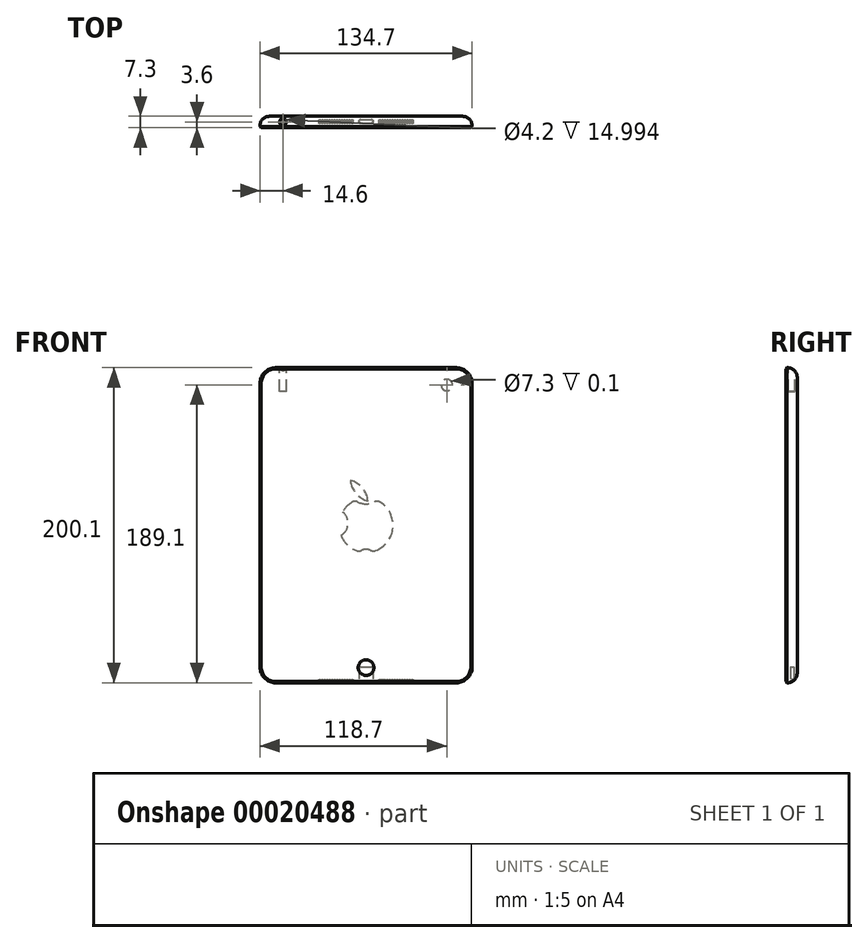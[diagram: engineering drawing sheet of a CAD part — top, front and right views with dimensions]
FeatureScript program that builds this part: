
annotation { "Feature Type Name" : "Feature", "Feature Type Description" : "" }
export const myFeature = defineFeature(function(context is Context, id is Id, definition is map)
    precondition{}
    {
        {
            var Q0;
            Q0=qCreatedBy(makeId("Front.planeOp"),FACE);
            var sketch = newSketch(context, id + "F0", { "sketchPlane" : qUnion([Q0])});
            skLineSegment(sketch, "E0.rect.bottom", {"start": v(-57.35, 100.05) * mm, "end": v(57.35, 100.05) * mm});
            skLineSegment(sketch, "E0.rect.top", {"start": v(-57.35, -100.05) * mm, "end": v(57.35, -100.05) * mm});
            skLineSegment(sketch, "E0.rect.left", {"start": v(-67.35, 90.05) * mm, "end": v(-67.35, -90.05) * mm});
            skLineSegment(sketch, "E0.rect.right", {"start": v(67.35, 90.05) * mm, "end": v(67.35, -90.05) * mm});
            skPoint(sketch, "E0.rect.middle", {"position": v(0, 0) * mm});
            skPoint(sketch, "E1.visualSharp", {"position": v(-67.35, 100.05) * mm});
            skArc(sketch, "E1.filletArc", {"start": v(-57.35, 100.05) * mm, "mid": v(-64.42, 97.12) * mm, "end": v(-67.35, 90.05) * mm});
            skPoint(sketch, "E2.visualSharp", {"position": v(67.35, 100.05) * mm});
            skArc(sketch, "E2.filletArc", {"start": v(67.35, 90.05) * mm, "mid": v(64.42, 97.12) * mm, "end": v(57.35, 100.05) * mm});
            skPoint(sketch, "E3.visualSharp", {"position": v(67.35, -100.05) * mm});
            skArc(sketch, "E3.filletArc", {"start": v(57.35, -100.05) * mm, "mid": v(64.42, -97.12) * mm, "end": v(67.35, -90.05) * mm});
            skPoint(sketch, "E4.visualSharp", {"position": v(-67.35, -100.05) * mm});
            skArc(sketch, "E4.filletArc", {"start": v(-67.35, -90.05) * mm, "mid": v(-64.42, -97.12) * mm, "end": v(-57.35, -100.05) * mm});
            skSolve(sketch);
        }
        {
            var Q0;
            Q0 = qSketchRegion(id + "F0", true);
            extrude(context, id + "F1", {"entities" : qUnion([Q0]), "endBound" : BoundingType.SYMMETRIC, "depth" : 7.2 * mm});
        }
        {
            var Q0;
            Q0=makeQuery(id+"F1.opExtrude","CAP_FACE",FACE,{"disambiguationData":[OSD([sQuery(id+"F0.wireOp",EDGE,"E0.rect.bottom"),sQuery(id+"F0.wireOp",EDGE,"E0.rect.top"),sQuery(id+"F0.wireOp",EDGE,"E0.rect.left"),sQuery(id+"F0.wireOp",EDGE,"E0.rect.right")])],"isStart":false});
            var sketch = newSketch(context, id + "F2", { "sketchPlane" : qUnion([Q0])});
            skLineSegment(sketch, "E5.rect.bottom", {"start": v(-60.65, 80.65) * mm, "end": v(60.65, 80.65) * mm});
            skLineSegment(sketch, "E5.rect.top", {"start": v(-60.65, -80.65) * mm, "end": v(60.65, -80.65) * mm});
            skLineSegment(sketch, "E5.rect.left", {"start": v(-60.65, 80.65) * mm, "end": v(-60.65, -80.65) * mm});
            skLineSegment(sketch, "E5.rect.right", {"start": v(60.65, 80.65) * mm, "end": v(60.65, -80.65) * mm});
            skPoint(sketch, "E5.rect.middle", {"position": v(0, 0) * mm});
            skCircle(sketch, "E6", {"center": v(0, 89.35) * mm, "radius": 1.2 * mm});
            skSolve(sketch);
        }
        {
            var Q0;
            Q0=makeQuery(id+"F2.imprint","IMPRINT",FACE,{"disambiguationData":[TD([[makeQuery(id+"F2.imprint","IMPRINT",EDGE,{"derivedFrom":sQuery(id+"F2.wireOp",EDGE,"E5.rect.bottom")}),-1.0]])]});
            var sketch = newSketch(context, id + "F3", { "sketchPlane" : qUnion([Q0])});
            skCircle(sketch, "E7", {"center": v(0, -90.45) * mm, "radius": 5 * mm});
            skSolve(sketch);
        }
        {
            var Q0;
            Q0=makeQuery(id+"F1.opExtrude","SWEPT_FACE",FACE,{"disambiguationData":[OSD([sQuery(id+"F0.wireOp",EDGE,"E0.rect.bottom")])]});
            var sketch = newSketch(context, id + "F4", { "sketchPlane" : qUnion([Q0])});
            skCircle(sketch, "E8", {"center": v(-52.75, 0) * mm, "radius": 2.1 * mm});
            skPoint(sketch, "E8.centerSnap0", {"position": v(57.35, 0) * mm});
            skSolve(sketch);
        }
        {
            var Q0;
            Q0=qCreatedBy(makeId("Top.planeOp"),FACE);
            cPlane(context, id + "F5", {"entities" : qUnion([Q0]), "cplaneType" : CPlaneType.OFFSET, "offset" : 90.45 * mm, "oppositeDirection" : true, "width" : 150 * mm, "height" : 150 * mm});
        }
        {
            var Q0;
            Q0=qCreatedBy(id+"F5.planeOp",FACE);
            var sketch = newSketch(context, id + "F6", { "sketchPlane" : qUnion([Q0])});
            skLineSegment(sketch, "E9.0", {"start": v(5, -3.6) * mm, "end": v(-5, -3.6) * mm});
            skArc(sketch, "E10", {"start": v(5, -3.6) * mm, "mid": v(2.51, -3.2) * mm, "end": v(0, -3.08) * mm});
            skLineSegment(sketch, "E11", {"start": v(0, -3.6) * mm, "end": v(0, -3.08) * mm});
            skLineSegment(sketch, "E12", {"start": v(0, -3.6) * mm, "end": v(5, -3.6) * mm});
            skSolve(sketch);
        }
        {
            var Q0;
            Q0=makeQuery(id+"F6.imprint","IMPRINT",FACE,{"disambiguationData":[TD([[makeQuery(id+"F6.imprint","IMPRINT",EDGE,{"derivedFrom":sQuery(id+"F6.wireOp",EDGE,"E10")}),1.0]])]});
            var Q1;
            Q1=sQuery(id+"F3.wireOp",EDGE,"E7");
            revolve(context, id + "F7", {"operationType" : NewBodyOperationType.REMOVE, "entities" : qUnion([Q0]), "axis" : qUnion([Q1]), "revolveType" : RevolveType.FULL, "oppositeDirection" : true});
        }
        {
            var Q0;
            Q0=makeQuery(id+"F1.opExtrude","CAP_FACE",FACE,{"disambiguationData":[OSD([sQuery(id+"F0.wireOp",EDGE,"E0.rect.bottom"),sQuery(id+"F0.wireOp",EDGE,"E0.rect.top"),sQuery(id+"F0.wireOp",EDGE,"E0.rect.left"),sQuery(id+"F0.wireOp",EDGE,"E0.rect.right"),sQuery(id+"F0.wireOp",EDGE,"E1.filletArc"),sQuery(id+"F0.wireOp",EDGE,"E2.filletArc"),sQuery(id+"F0.wireOp",EDGE,"E3.filletArc"),sQuery(id+"F0.wireOp",EDGE,"E4.filletArc")])],"isStart":true});
            var sketch = newSketch(context, id + "F8", { "sketchPlane" : qUnion([Q0])});
            skCircle(sketch, "E13", {"center": v(-51.35, 89.05) * mm, "radius": 3.65 * mm});
            skSolve(sketch);
        }
        {
            var Q0;
            Q0 = qSketchRegion(id + "F8", true);
            extrude(context, id + "F9", {"entities" : qUnion([Q0]), "operationType" : NewBodyOperationType.REMOVE, "oppositeDirection" : true, "depth" : 0.1 * mm});
        }
        {
            var Q0;
            Q0=makeQuery(id+"F1.opExtrude","CAP_EDGE",EDGE,{"disambiguationData":[OSD([sQuery(id+"F0.wireOp",EDGE,"E0.rect.left")])],"isStart":false});
            chamfer(context, id + "F10", {"entities" : qUnion([Q0]), "width" : 0.75 * mm, "tangentPropagation" : true});
        }
        {
            var Q0;
            Q0=makeQuery(id+"F1.opExtrude","CAP_EDGE",EDGE,{"disambiguationData":[OSD([sQuery(id+"F0.wireOp",EDGE,"E0.rect.bottom")])],"isStart":true});
            var Q1;
            Q1=makeQuery(id+"F1.opExtrude","CAP_EDGE",EDGE,{"disambiguationData":[OSD([sQuery(id+"F0.wireOp",EDGE,"E0.rect.left")])],"isStart":true});
            var Q2;
            Q2=makeQuery(id+"F1.opExtrude","CAP_EDGE",EDGE,{"disambiguationData":[OSD([sQuery(id+"F0.wireOp",EDGE,"E0.rect.right")])],"isStart":true});
            var Q3;
            Q3=makeQuery(id+"F1.opExtrude","CAP_EDGE",EDGE,{"disambiguationData":[OSD([sQuery(id+"F0.wireOp",EDGE,"E0.rect.top")])],"isStart":true});
            fillet(context, id + "F11", {"entities" : qUnion([Q0, Q1, Q2, Q3]), "radius" : 6 * mm, "tangentPropagation" : true, "allowEdgeOverflow" : false});
        }
        {
            var Q0;
            Q0=makeQuery(id+"F1.opExtrude","SWEPT_FACE",FACE,{"disambiguationData":[OSD([sQuery(id+"F0.wireOp",EDGE,"E0.rect.top")])]});
            var sketch = newSketch(context, id + "F12", { "sketchPlane" : qUnion([Q0])});
            skLineSegment(sketch, "E14.rect.bottom", {"start": v(-3.5, 0.85) * mm, "end": v(3.5, 0.85) * mm});
            skLineSegment(sketch, "E14.rect.top", {"start": v(-3.5, -1.45) * mm, "end": v(3.5, -1.45) * mm});
            skLineSegment(sketch, "E14.rect.left", {"start": v(-4.5, -0.15) * mm, "end": v(-4.5, -0.45) * mm});
            skLineSegment(sketch, "E14.rect.right", {"start": v(4.5, -0.15) * mm, "end": v(4.5, -0.45) * mm});
            skPoint(sketch, "E14.rect.middle", {"position": v(0, -0.3) * mm});
            skPoint(sketch, "E14.rect.middle.positionSnap0", {"position": v(0, 3.6) * mm});
            skPoint(sketch, "E14.rect.centerSnap0", {"position": v(0, 3.6) * mm});
            skPoint(sketch, "E15.visualSharp", {"position": v(-4.5, 0.85) * mm});
            skArc(sketch, "E15.filletArc", {"start": v(-3.5, 0.85) * mm, "mid": v(-4.2, 0.55) * mm, "end": v(-4.5, -0.15) * mm});
            skPoint(sketch, "E16.visualSharp", {"position": v(-4.5, -1.45) * mm});
            skArc(sketch, "E16.filletArc", {"start": v(-4.5, -0.45) * mm, "mid": v(-4.2, -1.16) * mm, "end": v(-3.5, -1.45) * mm});
            skPoint(sketch, "E17.visualSharp", {"position": v(4.5, 0.85) * mm});
            skArc(sketch, "E17.filletArc", {"start": v(4.5, -0.15) * mm, "mid": v(4.2, 0.55) * mm, "end": v(3.5, 0.85) * mm});
            skPoint(sketch, "E18.visualSharp", {"position": v(4.5, -1.45) * mm});
            skArc(sketch, "E18.filletArc", {"start": v(3.5, -1.45) * mm, "mid": v(4.2, -1.16) * mm, "end": v(4.5, -0.45) * mm});
            skSolve(sketch);
        }
        {
            var Q0;
            Q0=makeQuery(id+"F12.imprint","IMPRINT",FACE,{"disambiguationData":[TD([[makeQuery(id+"F12.imprint","IMPRINT",EDGE,{"derivedFrom":sQuery(id+"F12.wireOp",EDGE,"E14.rect.bottom")}),-1.0]])]});
            extrude(context, id + "F13", {"entities" : qUnion([Q0]), "operationType" : NewBodyOperationType.REMOVE, "oppositeDirection" : true, "depth" : 10 * mm});
        }
        {
            var Q0;
            Q0 = qSketchRegion(id + "F4", true);
            extrude(context, id + "F14", {"entities" : qUnion([Q0]), "operationType" : NewBodyOperationType.REMOVE, "oppositeDirection" : true, "depth" : 15 * mm});
        }
        {
            var Q0;
            {var subQ0=sQuery(id+"F0.wireOp",EDGE,"E0.rect.top");Q0=makeQuery(id+"F11.opFillet","BLEND_EDGE",EDGE,{"blendedFrom":[makeQuery(id+"F1.opExtrude","CAP_EDGE",EDGE,{"disambiguationData":[OSD([subQ0])],"isStart":true}),makeQuery(id+"F1.opExtrude","CAP_FACE",FACE,{"disambiguationData":[OSD([sQuery(id+"F0.wireOp",EDGE,"E0.rect.bottom"),subQ0,sQuery(id+"F0.wireOp",EDGE,"E0.rect.left"),sQuery(id+"F0.wireOp",EDGE,"E0.rect.right"),sQuery(id+"F0.wireOp",EDGE,"E1.filletArc"),sQuery(id+"F0.wireOp",EDGE,"E2.filletArc"),sQuery(id+"F0.wireOp",EDGE,"E3.filletArc"),sQuery(id+"F0.wireOp",EDGE,"E4.filletArc")])],"isStart":true})],"blendedInto":[makeQuery(id+"F1.opExtrude","CAP_FACE",FACE,{"disambiguationData":[OSD([sQuery(id+"F0.wireOp",EDGE,"E0.rect.bottom"),subQ0,sQuery(id+"F0.wireOp",EDGE,"E0.rect.left"),sQuery(id+"F0.wireOp",EDGE,"E0.rect.right"),sQuery(id+"F0.wireOp",EDGE,"E1.filletArc"),sQuery(id+"F0.wireOp",EDGE,"E2.filletArc"),sQuery(id+"F0.wireOp",EDGE,"E3.filletArc"),sQuery(id+"F0.wireOp",EDGE,"E4.filletArc")])],"isStart":true})]});}
            var Q1;
            {var subQ0=sQuery(id+"F0.wireOp",EDGE,"E0.rect.top");Q1=makeQuery(id+"F11.opFillet","BLEND_EDGE",EDGE,{"blendedFrom":[makeQuery(id+"F1.opExtrude","CAP_EDGE",EDGE,{"disambiguationData":[OSD([subQ0])],"isStart":true}),makeQuery(id+"F1.opExtrude","SWEPT_FACE",FACE,{"disambiguationData":[OSD([subQ0])]})],"blendedInto":[makeQuery(id+"F1.opExtrude","SWEPT_FACE",FACE,{"disambiguationData":[OSD([subQ0])]})]});}
            cPlane(context, id + "F15", {"entities" : qUnion([Q0, Q1]), "cplaneType" : CPlaneType.LINE_ANGLE, "offset" : 0 * mm, "angle" : 0 * degree, "width" : 150 * mm, "height" : 150 * mm});
        }
        {
            var Q0;
            Q0=qCreatedBy(id+"F15.planeOp",FACE);
            cPlane(context, id + "F16", {"entities" : qUnion([Q0]), "cplaneType" : CPlaneType.OFFSET, "offset" : 2 * mm, "width" : 150 * mm, "height" : 150 * mm});
        }
        {
            var Q0;
            Q0=qCreatedBy(id+"F16.planeOp",FACE);
            var sketch = newSketch(context, id + "F17", { "sketchPlane" : qUnion([Q0])});
            skEllipticalArc(sketch, "E19.0.0", {});
            skLineSegment(sketch, "E19.0.1", {"start": v(-67.35, -65.37) * mm, "end": v(-67.35, 61.98) * mm});
            skEllipticalArc(sketch, "E19.0.2", {});
            skLineSegment(sketch, "E19.0.3", {"start": v(-61.35, -61.13) * mm, "end": v(-61.35, 66.22) * mm});
            skLineSegment(sketch, "E20.0", {"start": v(67.35, 61.98) * mm, "end": v(67.35, -65.37) * mm});
            skLineSegment(sketch, "E21", {"start": v(0, -55.09) * mm, "end": v(0, -17.18) * mm, "construction": true});
            skLineSegment(sketch, "E22", {"start": v(-29.85, -36.59) * mm, "end": v(-29.85, -95.2) * mm, "construction": true});
            skLineSegment(sketch, "E23", {"start": v(-8.35, -35.36) * mm, "end": v(-8.35, -100.11) * mm, "construction": true});
            skLineSegment(sketch, "E24.MirrorCS", {"start": v(8.35, -35.36) * mm, "end": v(8.35, -100.11) * mm});
            skLineSegment(sketch, "E25.MirrorCS", {"start": v(29.85, -36.59) * mm, "end": v(29.85, -95.2) * mm});
            skLineSegment(sketch, "E26.0", {"start": v(3.5, -68.73) * mm, "end": v(-3.5, -68.73) * mm});
            skLineSegment(sketch, "E27.0", {"start": v(3.5, -71.2) * mm, "end": v(-3.5, -71.2) * mm});
            skLineSegment(sketch, "E28", {"start": v(-69.1, -68.73) * mm, "end": v(49.42, -68.73) * mm, "construction": true});
            skLineSegment(sketch, "E29", {"start": v(-71.16, -71.2) * mm, "end": v(65.79, -71.2) * mm, "construction": true});
            skCircle(sketch, "E30", {"center": v(-29.35, -69.23) * mm, "radius": 0.5 * mm});
            skCircle(sketch, "E31.1.0.0", {"center": v(-27.77, -69.23) * mm, "radius": 0.5 * mm});
            skCircle(sketch, "E31.2.0.0", {"center": v(-26.2, -69.23) * mm, "radius": 0.5 * mm});
            skCircle(sketch, "E31.3.0.0", {"center": v(-24.62, -69.23) * mm, "radius": 0.5 * mm});
            skCircle(sketch, "E31.4.0.0", {"center": v(-23.05, -69.23) * mm, "radius": 0.5 * mm});
            skCircle(sketch, "E31.5.0.0", {"center": v(-21.47, -69.23) * mm, "radius": 0.5 * mm});
            skCircle(sketch, "E31.6.0.0", {"center": v(-19.9, -69.23) * mm, "radius": 0.5 * mm});
            skCircle(sketch, "E31.7.0.0", {"center": v(-18.32, -69.23) * mm, "radius": 0.5 * mm});
            skCircle(sketch, "E31.8.0.0", {"center": v(-16.75, -69.23) * mm, "radius": 0.5 * mm});
            skCircle(sketch, "E31.9.0.0", {"center": v(-15.17, -69.23) * mm, "radius": 0.5 * mm});
            skCircle(sketch, "E31.10.0.0", {"center": v(-13.6, -69.23) * mm, "radius": 0.5 * mm});
            skCircle(sketch, "E31.11.0.0", {"center": v(-12.02, -69.23) * mm, "radius": 0.5 * mm});
            skCircle(sketch, "E31.12.0.0", {"center": v(-10.45, -69.23) * mm, "radius": 0.5 * mm});
            skCircle(sketch, "E31.13.0.0", {"center": v(-8.87, -69.23) * mm, "radius": 0.5 * mm});
            skLineSegment(sketch, "E31.direction1", {"start": v(-29.35, -69.23) * mm, "end": v(-27.77, -69.23) * mm, "construction": true});
            skLineSegment(sketch, "E32", {"start": v(-33, -69.96) * mm, "end": v(-5.17, -69.96) * mm, "construction": true});
            skCircle(sketch, "E33.MirrorC", {"center": v(-29.35, -70.7) * mm, "radius": 0.5 * mm});
            skCircle(sketch, "E34.MirrorC", {"center": v(-27.77, -70.7) * mm, "radius": 0.5 * mm});
            skCircle(sketch, "E35.MirrorC", {"center": v(-26.2, -70.7) * mm, "radius": 0.5 * mm});
            skCircle(sketch, "E36.MirrorC", {"center": v(-24.62, -70.7) * mm, "radius": 0.5 * mm});
            skCircle(sketch, "E37.MirrorC", {"center": v(-23.05, -70.7) * mm, "radius": 0.5 * mm});
            skCircle(sketch, "E38.MirrorC", {"center": v(-21.47, -70.7) * mm, "radius": 0.5 * mm});
            skCircle(sketch, "E39.MirrorC", {"center": v(-19.9, -70.7) * mm, "radius": 0.5 * mm});
            skCircle(sketch, "E40.MirrorC", {"center": v(-18.32, -70.7) * mm, "radius": 0.5 * mm});
            skCircle(sketch, "E41.MirrorC", {"center": v(-16.75, -70.7) * mm, "radius": 0.5 * mm});
            skCircle(sketch, "E42.MirrorC", {"center": v(-15.17, -70.7) * mm, "radius": 0.5 * mm});
            skCircle(sketch, "E43.MirrorC", {"center": v(-13.6, -70.7) * mm, "radius": 0.5 * mm});
            skCircle(sketch, "E44.MirrorC", {"center": v(-12.02, -70.7) * mm, "radius": 0.5 * mm});
            skCircle(sketch, "E45.MirrorC", {"center": v(-10.45, -70.7) * mm, "radius": 0.5 * mm});
            skCircle(sketch, "E46.MirrorC", {"center": v(-8.87, -70.7) * mm, "radius": 0.5 * mm});
            skCircle(sketch, "E47.MirrorC", {"center": v(8.87, -69.23) * mm, "radius": 0.5 * mm});
            skCircle(sketch, "E48.MirrorC", {"center": v(29.35, -69.23) * mm, "radius": 0.5 * mm});
            skCircle(sketch, "E49.MirrorC", {"center": v(10.45, -69.23) * mm, "radius": 0.5 * mm});
            skCircle(sketch, "E50.MirrorC", {"center": v(12.02, -69.23) * mm, "radius": 0.5 * mm});
            skCircle(sketch, "E51.MirrorC", {"center": v(27.77, -69.23) * mm, "radius": 0.5 * mm});
            skCircle(sketch, "E52.MirrorC", {"center": v(19.9, -69.23) * mm, "radius": 0.5 * mm});
            skCircle(sketch, "E53.MirrorC", {"center": v(24.62, -69.23) * mm, "radius": 0.5 * mm});
            skCircle(sketch, "E54.MirrorC", {"center": v(16.75, -69.23) * mm, "radius": 0.5 * mm});
            skCircle(sketch, "E55.MirrorC", {"center": v(13.6, -69.23) * mm, "radius": 0.5 * mm});
            skCircle(sketch, "E56.MirrorC", {"center": v(26.2, -69.23) * mm, "radius": 0.5 * mm});
            skCircle(sketch, "E57.MirrorC", {"center": v(21.47, -69.23) * mm, "radius": 0.5 * mm});
            skCircle(sketch, "E58.MirrorC", {"center": v(15.17, -69.23) * mm, "radius": 0.5 * mm});
            skCircle(sketch, "E59.MirrorC", {"center": v(23.05, -69.23) * mm, "radius": 0.5 * mm});
            skCircle(sketch, "E60.MirrorC", {"center": v(18.32, -69.23) * mm, "radius": 0.5 * mm});
            skLineSegment(sketch, "E61.MirrorCS", {"start": v(29.35, -69.23) * mm, "end": v(27.77, -69.23) * mm});
            skCircle(sketch, "E62.MirrorC", {"center": v(26.2, -70.7) * mm, "radius": 0.5 * mm});
            skCircle(sketch, "E63.MirrorC", {"center": v(29.35, -70.7) * mm, "radius": 0.5 * mm});
            skCircle(sketch, "E64.MirrorC", {"center": v(27.77, -70.7) * mm, "radius": 0.5 * mm});
            skCircle(sketch, "E65.MirrorC", {"center": v(8.87, -70.7) * mm, "radius": 0.5 * mm});
            skCircle(sketch, "E66.MirrorC", {"center": v(24.62, -70.7) * mm, "radius": 0.5 * mm});
            skCircle(sketch, "E67.MirrorC", {"center": v(16.75, -70.7) * mm, "radius": 0.5 * mm});
            skCircle(sketch, "E68.MirrorC", {"center": v(10.45, -70.7) * mm, "radius": 0.5 * mm});
            skCircle(sketch, "E69.MirrorC", {"center": v(18.32, -70.7) * mm, "radius": 0.5 * mm});
            skCircle(sketch, "E70.MirrorC", {"center": v(21.47, -70.7) * mm, "radius": 0.5 * mm});
            skCircle(sketch, "E71.MirrorC", {"center": v(12.02, -70.7) * mm, "radius": 0.5 * mm});
            skCircle(sketch, "E72.MirrorC", {"center": v(19.9, -70.7) * mm, "radius": 0.5 * mm});
            skCircle(sketch, "E73.MirrorC", {"center": v(15.17, -70.7) * mm, "radius": 0.5 * mm});
            skCircle(sketch, "E74.MirrorC", {"center": v(13.6, -70.7) * mm, "radius": 0.5 * mm});
            skCircle(sketch, "E75.MirrorC", {"center": v(23.05, -70.7) * mm, "radius": 0.5 * mm});
            const initialGuessF17  = {"E19.0.0": [-0.06135, 0.06197790937100092, -1, 0, 0.006, 0.004242640687119283, 4.71238898038469, 0], "E19.0.2": [-0.06135, -0.06537202192069634, 1, 0, 0.006, 0.004242640687119283, 1.5707963267948966, 3.141592653589793]};
            skSetInitialGuess(sketch, initialGuessF17);
            skSolve(sketch);
        }
        {
            var Q0;
            Q0 = qSketchRegion(id + "F17", true);
            extrude(context, id + "F18", {"entities" : qUnion([Q0]), "operationType" : NewBodyOperationType.REMOVE, "oppositeDirection" : true, "depth" : 1.5 * mm});
        }
        {
            var Q0;
            Q0=makeQuery(id+"F1.opExtrude","CAP_FACE",FACE,{"disambiguationData":[OSD([sQuery(id+"F0.wireOp",EDGE,"E0.rect.bottom"),sQuery(id+"F0.wireOp",EDGE,"E0.rect.top"),sQuery(id+"F0.wireOp",EDGE,"E0.rect.left"),sQuery(id+"F0.wireOp",EDGE,"E0.rect.right"),sQuery(id+"F0.wireOp",EDGE,"E1.filletArc"),sQuery(id+"F0.wireOp",EDGE,"E2.filletArc"),sQuery(id+"F0.wireOp",EDGE,"E3.filletArc"),sQuery(id+"F0.wireOp",EDGE,"E4.filletArc")])],"isStart":true});
            var sketch = newSketch(context, id + "F19", { "sketchPlane" : qUnion([Q0])});
            skArc(sketch, "E76", {"start": v(14.93, 8.5) * mm, "mid": v(12.4, 11.89) * mm, "end": v(9.12, 14.56) * mm});
            skArc(sketch, "E77", {"start": v(14.93, 8.5) * mm, "mid": v(11.4, 0.76) * mm, "end": v(15.92, -6.46) * mm});
            skArc(sketch, "E78", {"start": v(2.9, -15.94) * mm, "mid": v(0, -15.28) * mm, "end": v(-2.9, -15.94) * mm});
            skArc(sketch, "E79.trimOffspring", {"start": v(6.04, -16.08) * mm, "mid": v(11.99, -12.3) * mm, "end": v(15.92, -6.46) * mm});
            skPoint(sketch, "E80.visualSharp", {"position": v(-4.09, -16.69) * mm});
            skArc(sketch, "E80.filletArc", {"start": v(-6.04, -16.08) * mm, "mid": v(-4.45, -16.33) * mm, "end": v(-2.9, -15.94) * mm});
            skPoint(sketch, "E81.visualSharp", {"position": v(4.09, -16.69) * mm});
            skArc(sketch, "E81.filletArc", {"start": v(2.9, -15.94) * mm, "mid": v(4.45, -16.33) * mm, "end": v(6.04, -16.08) * mm});
            skArc(sketch, "E82", {"start": v(-5.25, 14.77) * mm, "mid": v(0, 13.57) * mm, "end": v(5.25, 14.77) * mm});
            skArc(sketch, "E83.trimOffspring", {"start": v(-9.12, 14.56) * mm, "mid": v(-17.1, -1.72) * mm, "end": v(-6.04, -16.08) * mm});
            skPoint(sketch, "E84.visualSharp", {"position": v(-6.9, 15.73) * mm});
            skArc(sketch, "E84.filletArc", {"start": v(-5.25, 14.77) * mm, "mid": v(-7.21, 15.16) * mm, "end": v(-9.12, 14.56) * mm});
            skPoint(sketch, "E85.visualSharp", {"position": v(6.9, 15.73) * mm});
            skArc(sketch, "E85.filletArc", {"start": v(9.12, 14.56) * mm, "mid": v(7.21, 15.16) * mm, "end": v(5.25, 14.77) * mm});
            skArc(sketch, "E86", {"start": v(9.85, 28.44) * mm, "mid": v(2.2, 23.7) * mm, "end": v(-1.21, 15.39) * mm});
            skArc(sketch, "E87", {"start": v(-1.21, 15.39) * mm, "mid": v(6.44, 20.12) * mm, "end": v(9.85, 28.44) * mm});
            skSolve(sketch);
        }
        {
            var Q0;
            Q0 = qSketchRegion(id + "F19", true);
            extrude(context, id + "F20", {"entities" : qUnion([Q0]), "operationType" : NewBodyOperationType.ADD, "depth" : 0.1 * mm});
        }
    });
